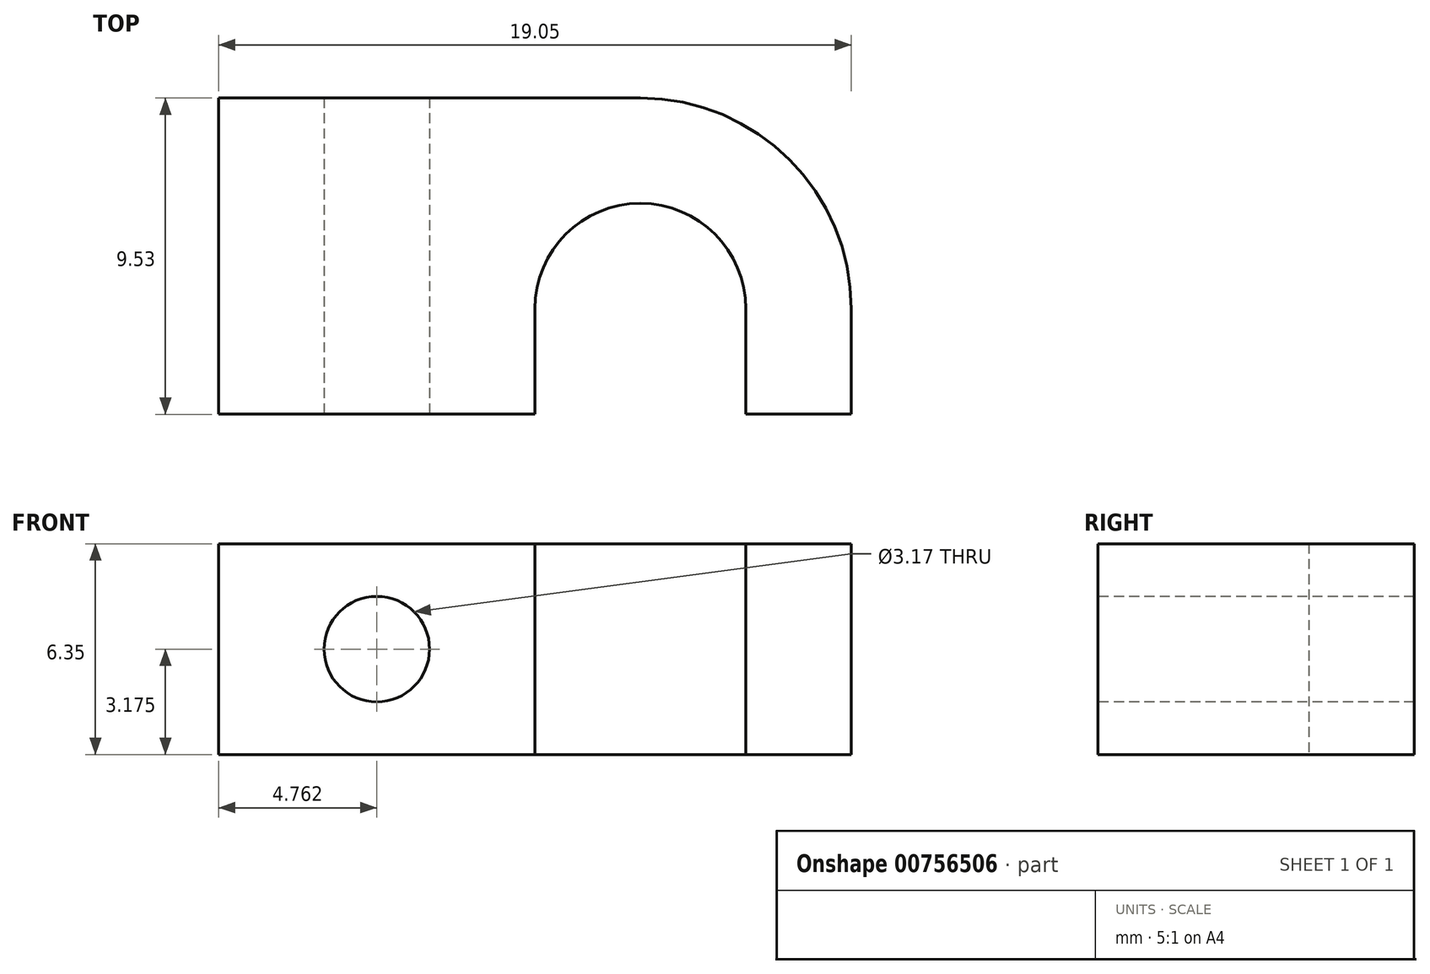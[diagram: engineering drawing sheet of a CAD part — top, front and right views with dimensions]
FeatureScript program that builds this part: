
annotation { "Feature Type Name" : "Feature", "Feature Type Description" : "" }
export const myFeature = defineFeature(function(context is Context, id is Id, definition is map)
    precondition{}
    {
        {
            assignVariable(context, id + "F0", {"name" : "clipWidth", "anyValue" : 6.35 * mm});
        }
        {
            var Q0;
            Q0=qCreatedBy(makeId("Top.planeOp"),FACE);
            var sketch = newSketch(context, id + "F1", { "sketchPlane" : qUnion([Q0])});
            skArc(sketch, "E0", {"start": v(3.18, 0) * mm, "mid": v(0, 3.18) * mm, "end": v(-3.18, 0) * mm});
            skArc(sketch, "E1.0", {"start": v(6.35, 0) * mm, "mid": v(4.5, 4.5) * mm, "end": v(0, 6.35) * mm});
            skLineSegment(sketch, "E2", {"start": v(6.35, -3.17) * mm, "end": v(3.18, -3.17) * mm});
            skLineSegment(sketch, "E3", {"start": v(6.35, 0) * mm, "end": v(6.35, -3.17) * mm});
            skLineSegment(sketch, "E4", {"start": v(3.18, 0) * mm, "end": v(3.18, -3.17) * mm});
            skLineSegment(sketch, "E5", {"start": v(-3.18, 0) * mm, "end": v(-3.18, -3.18) * mm});
            skLineSegment(sketch, "E6", {"start": v(-6.35, 6.35) * mm, "end": v(-6.35, -3.18) * mm});
            skLineSegment(sketch, "E7.trimOffspring", {"start": v(-3.18, -3.18) * mm, "end": v(-12.7, -3.18) * mm});
            skLineSegment(sketch, "E8", {"start": v(0, 6.35) * mm, "end": v(-12.7, 6.35) * mm});
            skLineSegment(sketch, "E9", {"start": v(-9.53, 6.35) * mm, "end": v(-9.53, -3.18) * mm});
            skLineSegment(sketch, "E10", {"start": v(-12.7, 6.35) * mm, "end": v(-12.7, -3.18) * mm});
            skSolve(sketch);
        }
        {
            var Q0;
            {var subQ2=sQuery(id+"F1.wireOp",EDGE,"E9");Q0=makeQuery(id+"F1.imprint","IMPRINT",FACE,{"disambiguationData":[TD([[makeQuery(id+"F1.imprint","IMPRINT",EDGE,{"derivedFrom":subQ2}),-1.0]])]});}
            var Q1;
            {var subQ0=sQuery(id+"F1.wireOp",EDGE,"E6");Q1=makeQuery(id+"F1.imprint","IMPRINT",FACE,{"disambiguationData":[TD([[makeQuery(id+"F1.imprint","IMPRINT",EDGE,{"derivedFrom":subQ0}),-1.0]])]});}
            var Q2;
            Q2=makeQuery(id+"F1.imprint","IMPRINT",FACE,{"disambiguationData":[TD([[makeQuery(id+"F1.imprint","IMPRINT",EDGE,{"derivedFrom":sQuery(id+"F1.wireOp",EDGE,"E0")}),-1.0]])]});
            extrude(context, id + "F2", {"entities" : qUnion([Q0, Q1, Q2]), "depth" : getVariable(context, 'clipWidth'), "offsetDistance" : 25.4 * mm});
        }
        {
            var Q0;
            Q0=makeQuery(id+"F2.opExtrude","SWEPT_FACE",FACE,{"disambiguationData":[OSD([sQuery(id+"F1.wireOp",EDGE,"E7.trimOffspring")])]});
            var sketch = newSketch(context, id + "F3", { "sketchPlane" : qUnion([Q0])});
            skLineSegment(sketch, "E11", {"start": v(-3.18, 6.35) * mm, "end": v(-12.7, 0) * mm, "construction": true});
            skCircle(sketch, "E12", {"center": v(-7.94, 3.18) * mm, "radius": 1.59 * mm});
            skSolve(sketch);
        }
        {
            var Q0;
            Q0=makeQuery(id+"F3.imprint","IMPRINT",FACE,{"disambiguationData":[TD([[makeQuery(id+"F3.imprint","IMPRINT",EDGE,{"derivedFrom":sQuery(id+"F3.wireOp",EDGE,"E12")}),1.0]])]});
            var Q1;
            Q1=makeQuery(id+"F2.opExtrude","SWEPT_FACE",FACE,{"disambiguationData":[OSD([sQuery(id+"F1.wireOp",EDGE,"E8")])]});
            extrude(context, id + "F4", {"entities" : qUnion([Q0]), "operationType" : NewBodyOperationType.REMOVE, "endBound" : BoundingType.UP_TO_SURFACE, "oppositeDirection" : true, "depth" : 25.4 * mm, "endBoundEntityFace" : qUnion([Q1]), "offsetDistance" : 25.4 * mm});
        }
    });
